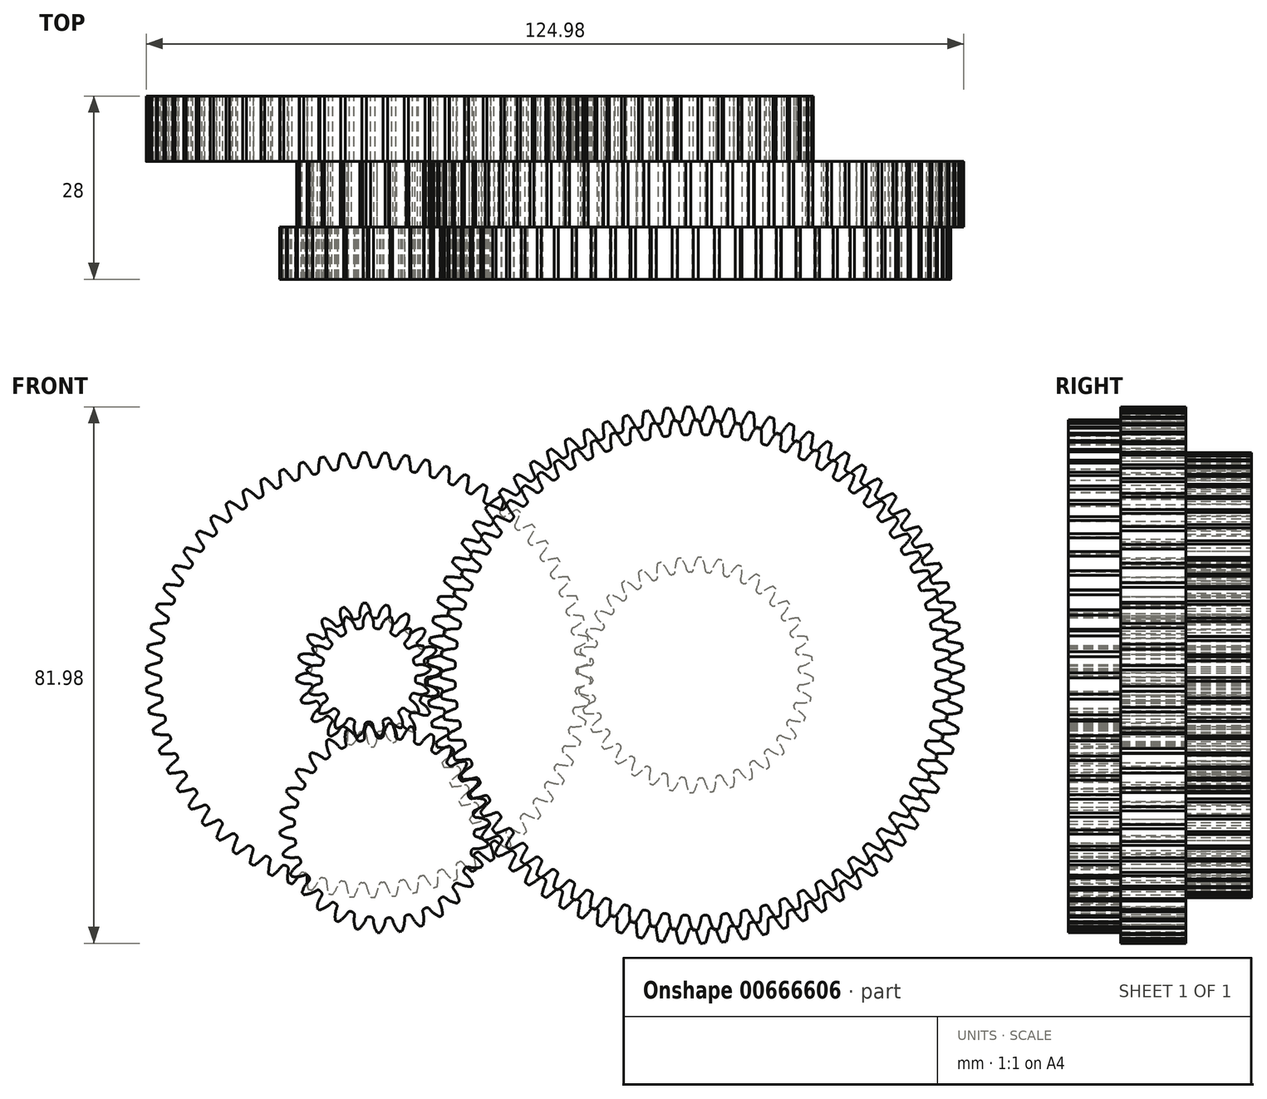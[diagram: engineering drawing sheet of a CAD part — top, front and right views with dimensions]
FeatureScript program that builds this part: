
annotation { "Feature Type Name" : "Feature", "Feature Type Description" : "" }
export const myFeature = defineFeature(function(context is Context, id is Id, definition is map)
    precondition{}
    {
        {
            var Q0;
            Q0=qCreatedBy(makeId("Front.planeOp"),FACE);
            var sketch = newSketch(context, id + "F0", { "sketchPlane" : qUnion([Q0])});
            skLineSegment(sketch, "E0", {"start": v(0, 0) * mm, "end": v(-50, 0) * mm, "construction": true});
            skLineSegment(sketch, "E1", {"start": v(-25, 25) * mm, "end": v(-25, -25) * mm, "construction": true});
            skPoint(sketch, "E2", {"position": v(-25, 0) * mm});
            skLineSegment(sketch, "E3", {"start": v(0, -50) * mm, "end": v(0, 50) * mm, "construction": true});
            skPoint(sketch, "E4", {"position": v(0, 0) * mm});
            skLineSegment(sketch, "E5.MirrorCS", {"start": v(25, 25) * mm, "end": v(25, -25) * mm, "construction": true});
            skLineSegment(sketch, "E6.MirrorCS", {"start": v(0, 0) * mm, "end": v(50, 0) * mm, "construction": true});
            skPoint(sketch, "E7.MirrorP", {"position": v(25, 0) * mm});
            skSolve(sketch);
        }
        {
            var Q0;
            Q0=qCreatedBy(makeId("Front.planeOp"),FACE);
            cPlane(context, id + "F1", {"entities" : qUnion([Q0]), "cplaneType" : CPlaneType.OFFSET, "offset" : 0 * mm, "width" : 150 * mm, "height" : 150 * mm});
        }
        {
            var Q0;
            Q0=qCreatedBy(makeId("Front.planeOp"),FACE);
            cPlane(context, id + "F2", {"entities" : qUnion([Q0]), "cplaneType" : CPlaneType.OFFSET, "offset" : 10 * mm, "width" : 150 * mm, "height" : 150 * mm});
        }
        {
            var Q0;
            Q0=qCreatedBy(id+"F2.planeOp",FACE);
            var sketch = newSketch(context, id + "F3", { "sketchPlane" : qUnion([Q0])});
            skCircle(sketch, "E8", {"center": v(25, 0) * mm, "radius": 17 * mm, "construction": true});
            skCircle(sketch, "E9", {"center": v(-25, 0) * mm, "radius": 33 * mm, "construction": true});
            skLineSegment(sketch, "E10", {"start": v(-25, 0) * mm, "end": v(-25, 41.53) * mm, "construction": true});
            skLineSegment(sketch, "E11", {"start": v(-25, 33) * mm, "end": v(-54.6, 33) * mm, "construction": true});
            skLineSegment(sketch, "E12", {"start": v(-25, 33) * mm, "end": v(-54.83, 22.14) * mm, "construction": true});
            skLineSegment(sketch, "E13", {"start": v(-35.6, 29.14) * mm, "end": v(-25, 0) * mm, "construction": true});
            skCircle(sketch, "E14", {"center": v(-25, 0) * mm, "radius": 31.75 * mm});
            skPoint(sketch, "E15", {"position": v(-25, 31.75) * mm});
            skPoint(sketch, "E16", {"position": v(-25, 34) * mm});
            skPoint(sketch, "E17", {"position": v(-25, 33.25) * mm});
            skLineSegment(sketch, "E18", {"start": v(-35.6, 29.14) * mm, "end": v(-25, 33.25) * mm, "construction": true});
            skPoint(sketch, "E19", {"position": v(-32.95, 30.17) * mm});
            skArc(sketch, "E20", {"start": v(-25.33, 34) * mm, "mid": v(-41.15, 27.8) * mm, "end": v(-24.46, 31) * mm, "construction": true});
            skArc(sketch, "E21", {"start": v(-24.46, 31) * mm, "mid": v(-24.76, 32.54) * mm, "end": v(-25.33, 34) * mm});
            skPoint(sketch, "E22", {"position": v(-24.9, 33) * mm});
            skPoint(sketch, "E23", {"position": v(-25.64, 33) * mm});
            skLineSegment(sketch, "E24", {"start": v(-25.64, 33) * mm, "end": v(-25, 0) * mm, "construction": true});
            skArc(sketch, "E25.MirrorCS", {"start": v(-26.74, 30.96) * mm, "mid": v(-26.5, 32.5) * mm, "end": v(-26, 33.99) * mm});
            skArc(sketch, "E26", {"start": v(-26, 33.99) * mm, "mid": v(-24.34, -34) * mm, "end": v(-25.33, 34) * mm, "construction": true});
            skArc(sketch, "E27", {"start": v(-25.33, 34) * mm, "mid": v(-25.66, 34) * mm, "end": v(-26, 33.99) * mm});
            skArc(sketch, "E28", {"start": v(-26.74, 30.96) * mm, "mid": v(-24.4, -31) * mm, "end": v(-24.46, 31) * mm});
            skArc(sketch, "E29", {"start": v(-24.46, 31) * mm, "mid": v(-25.6, 31) * mm, "end": v(-26.74, 30.96) * mm, "construction": true});
            skLineSegment(sketch, "E30", {"start": v(25, 0) * mm, "end": v(25, 21.62) * mm, "construction": true});
            skLineSegment(sketch, "E31", {"start": v(25, 17) * mm, "end": v(45.36, 17) * mm});
            skLineSegment(sketch, "E32", {"start": v(25, 17) * mm, "end": v(45.36, 9.59) * mm, "construction": true});
            skLineSegment(sketch, "E33", {"start": v(30.46, 15.01) * mm, "end": v(25, 0) * mm, "construction": true});
            skCircle(sketch, "E34", {"center": v(25, 0) * mm, "radius": 15.97 * mm, "construction": true});
            skPoint(sketch, "E35", {"position": v(25, 18) * mm});
            skPoint(sketch, "E36", {"position": v(25, 15.97) * mm});
            skPoint(sketch, "E37", {"position": v(25, 17.33) * mm});
            skLineSegment(sketch, "E38", {"start": v(25, 17.33) * mm, "end": v(30.46, 15.01) * mm, "construction": true});
            skPoint(sketch, "E39", {"position": v(29.1, 15.59) * mm});
            skPoint(sketch, "E40", {"position": v(24.88, 17) * mm});
            skPoint(sketch, "E41", {"position": v(25.61, 16.99) * mm});
            skLineSegment(sketch, "E42", {"start": v(25.61, 16.99) * mm, "end": v(25, 0) * mm, "construction": true});
            skArc(sketch, "E43", {"start": v(25.35, 18) * mm, "mid": v(24.85, 16.92) * mm, "end": v(24.65, 15.75) * mm});
            skArc(sketch, "E44", {"start": v(24.65, 15.75) * mm, "mid": v(33.34, 14.26) * mm, "end": v(25.35, 18) * mm, "construction": true});
            skArc(sketch, "E45.MirrorCS", {"start": v(25.94, 17.98) * mm, "mid": v(26.37, 16.86) * mm, "end": v(26.48, 15.68) * mm});
            skArc(sketch, "E46", {"start": v(25.94, 17.98) * mm, "mid": v(25.65, 17.99) * mm, "end": v(25.35, 18) * mm});
            skArc(sketch, "E47", {"start": v(25.35, 18) * mm, "mid": v(24.35, -17.99) * mm, "end": v(25.94, 17.98) * mm, "construction": true});
            skArc(sketch, "E48", {"start": v(24.65, 15.75) * mm, "mid": v(24.43, -15.74) * mm, "end": v(26.48, 15.68) * mm});
            skArc(sketch, "E49", {"start": v(26.48, 15.68) * mm, "mid": v(25.57, 15.74) * mm, "end": v(24.65, 15.75) * mm, "construction": true});
            skSolve(sketch);
        }
        {
            var Q0;
            Q0=makeQuery(id+"F3.imprint","IMPRINT",FACE,{"disambiguationData":[TD([[makeQuery(id+"F3.imprint","IMPRINT",EDGE,{"derivedFrom":sQuery(id+"F3.wireOp",EDGE,"E21")}),1.0]])]});
            var Q1;
            Q1=makeQuery(id+"F3.imprint","IMPRINT",FACE,{"disambiguationData":[TD([[makeQuery(id+"F3.imprint","IMPRINT",EDGE,{"derivedFrom":sQuery(id+"F3.wireOp",EDGE,"E43")}),1.0]])]});
            var Q2;
            {var subQ0=sQuery(id+"F3.wireOp",EDGE,"E28");Q2=makeQuery(id+"F3.imprint","IMPRINT",FACE,{"disambiguationData":[TD([[makeQuery(id+"F3.imprint","IMPRINT",EDGE,{"derivedFrom":subQ0}),-1.0]])]});}
            extrude(context, id + "F4", {"entities" : qUnion([Q0, Q1, Q2]), "depth" : 10 * mm, "offsetDistance" : 25 * mm});
        }
        {
            var Q0;
            Q0=makeQuery(id+"F4.opExtrude","SWEPT_EDGE",EDGE,{"disambiguationData":[OSD([sQuery(id+"F3.wireOp",EDGE,"E14"),sQuery(id+"F3.wireOp",EDGE,"E21")])]});
            var Q1;
            Q1=makeQuery(id+"F4.opExtrude","SWEPT_EDGE",EDGE,{"disambiguationData":[OSD([sQuery(id+"F3.wireOp",EDGE,"E14"),sQuery(id+"F3.wireOp",EDGE,"E25.MirrorCS")])]});
            var Q2;
            Q2=makeQuery(id+"F4.opExtrude","SWEPT_EDGE",EDGE,{"disambiguationData":[OSD([sQuery(id+"F3.wireOp",EDGE,"E45.MirrorCS"),sQuery(id+"F3.wireOp",EDGE,"E48")])]});
            var Q3;
            Q3=makeQuery(id+"F4.opExtrude","SWEPT_EDGE",EDGE,{"disambiguationData":[OSD([sQuery(id+"F3.wireOp",EDGE,"E43"),sQuery(id+"F3.wireOp",EDGE,"E48")])]});
            fillet(context, id + "F5", {"entities" : qUnion([Q0, Q1, Q2, Q3]), "radius" : 0.45 * mm, "tangentPropagation" : true, "allowEdgeOverflow" : false});
        }
        {
            var Q0;
            Q0=makeQuery(id+"F4.opExtrude","SWEPT_BODY",BODY,{"disambiguationData":[OSD([sQuery(id+"F3.wireOp",EDGE,"E43"),sQuery(id+"F3.wireOp",EDGE,"E45.MirrorCS"),sQuery(id+"F3.wireOp",EDGE,"E46"),sQuery(id+"F3.wireOp",EDGE,"E48")])]});
            var Q1;
            Q1=makeQuery(id+"F4.opExtrude","SWEPT_FACE",FACE,{"disambiguationData":[OSD([sQuery(id+"F3.wireOp",EDGE,"E48")])]});
            circularPattern(context, id + "F6", {"operationType" : NewBodyOperationType.ADD, "entities" : qUnion([Q0]), "axis" : qUnion([Q1]), "angle" : 360 * degree, "instanceCount" : 36, "equalSpace" : true});
        }
        {
            var Q0;
            Q0=makeQuery(id+"F4.opExtrude","SWEPT_BODY",BODY,{"disambiguationData":[OSD([sQuery(id+"F3.wireOp",EDGE,"E14"),sQuery(id+"F3.wireOp",EDGE,"E21"),sQuery(id+"F3.wireOp",EDGE,"E25.MirrorCS"),sQuery(id+"F3.wireOp",EDGE,"E27")])]});
            var Q1;
            Q1=makeQuery(id+"F4.opExtrude","SWEPT_FACE",FACE,{"disambiguationData":[OSD([sQuery(id+"F3.wireOp",EDGE,"E14")])]});
            circularPattern(context, id + "F7", {"operationType" : NewBodyOperationType.ADD, "entities" : qUnion([Q0]), "axis" : qUnion([Q1]), "angle" : 360 * degree, "instanceCount" : 66, "equalSpace" : true});
        }
        {
            var Q0;
            Q0=qCreatedBy(makeId("Front.planeOp"),FACE);
            cPlane(context, id + "F8", {"entities" : qUnion([Q0]), "cplaneType" : CPlaneType.OFFSET, "offset" : 20 * mm, "width" : 150 * mm, "height" : 150 * mm});
        }
        {
            var Q0;
            Q0=qCreatedBy(id+"F8.planeOp",FACE);
            var sketch = newSketch(context, id + "F9", { "sketchPlane" : qUnion([Q0])});
            skCircle(sketch, "E50", {"center": v(-25, 0) * mm, "radius": 10 * mm, "construction": true});
            skCircle(sketch, "E51", {"center": v(25, 0) * mm, "radius": 40 * mm, "construction": true});
            skLineSegment(sketch, "E52", {"start": v(-25, 0) * mm, "end": v(-25, 15.82) * mm, "construction": true});
            skLineSegment(sketch, "E53", {"start": v(-25, 10) * mm, "end": v(-43.04, 10) * mm, "construction": true});
            skLineSegment(sketch, "E54", {"start": v(-25, 10) * mm, "end": v(-43.04, 3.43) * mm, "construction": true});
            skCircle(sketch, "E55", {"center": v(-25, 0) * mm, "radius": 9.4 * mm, "construction": true});
            skLineSegment(sketch, "E56", {"start": v(-25, 0) * mm, "end": v(-28.21, 8.83) * mm, "construction": true});
            skPoint(sketch, "E57", {"position": v(-25, 11) * mm});
            skPoint(sketch, "E58", {"position": v(-25, 9.4) * mm});
            skPoint(sketch, "E59", {"position": v(-25, 10.47) * mm});
            skLineSegment(sketch, "E60", {"start": v(-25, 10.47) * mm, "end": v(-28.21, 8.83) * mm, "construction": true});
            skPoint(sketch, "E61", {"position": v(-27.41, 9.24) * mm});
            skArc(sketch, "E62", {"start": v(-25.35, 11) * mm, "mid": v(-30.02, 8.54) * mm, "end": v(-24.75, 8.75) * mm, "construction": true});
            skArc(sketch, "E63", {"start": v(-24.75, 8.75) * mm, "mid": v(-24.8, 9.94) * mm, "end": v(-25.35, 11) * mm});
            skPoint(sketch, "E64", {"position": v(-24.81, 10) * mm});
            skPoint(sketch, "E65", {"position": v(-25.55, 9.98) * mm});
            skLineSegment(sketch, "E66", {"start": v(-25.55, 9.98) * mm, "end": v(-25, 0) * mm, "construction": true});
            skArc(sketch, "E67.MirrorCS", {"start": v(-26.2, 8.67) * mm, "mid": v(-26.3, 9.86) * mm, "end": v(-25.86, 10.97) * mm});
            skArc(sketch, "E68", {"start": v(-26.2, 8.67) * mm, "mid": v(-24.52, -8.74) * mm, "end": v(-24.75, 8.75) * mm});
            skArc(sketch, "E69", {"start": v(-24.75, 8.75) * mm, "mid": v(-25.48, 8.74) * mm, "end": v(-26.2, 8.67) * mm, "construction": true});
            skArc(sketch, "E70", {"start": v(-25.35, 11) * mm, "mid": v(-25.6, 10.98) * mm, "end": v(-25.86, 10.97) * mm});
            skArc(sketch, "E71", {"start": v(-25.86, 10.97) * mm, "mid": v(-24.4, -10.98) * mm, "end": v(-25.35, 11) * mm, "construction": true});
            skLineSegment(sketch, "E72", {"start": v(25, 0) * mm, "end": v(26.56, 44.58) * mm, "construction": true});
            skLineSegment(sketch, "E73", {"start": v(26.4, 39.98) * mm, "end": v(67.67, 39.98) * mm, "construction": true});
            skLineSegment(sketch, "E74", {"start": v(26.4, 39.98) * mm, "end": v(67.67, 24.95) * mm, "construction": true});
            skLineSegment(sketch, "E75", {"start": v(38.01, 35.75) * mm, "end": v(25, 0) * mm, "construction": true});
            skCircle(sketch, "E76", {"center": v(25, 0) * mm, "radius": 38.75 * mm});
            skPoint(sketch, "E77", {"position": v(26.35, 38.73) * mm});
            skPoint(sketch, "E78", {"position": v(26.43, 40.98) * mm});
            skPoint(sketch, "E79", {"position": v(26.4, 40.23) * mm});
            skLineSegment(sketch, "E80", {"start": v(26.4, 40.23) * mm, "end": v(38.01, 35.75) * mm, "construction": true});
            skPoint(sketch, "E81", {"position": v(34.8, 36.99) * mm});
            skArc(sketch, "E82", {"start": v(26.73, 40.96) * mm, "mid": v(26.17, 39.54) * mm, "end": v(25.86, 38.03) * mm});
            skArc(sketch, "E83", {"start": v(25.86, 38.03) * mm, "mid": v(43.43, 34.44) * mm, "end": v(26.73, 40.96) * mm, "construction": true});
            skPoint(sketch, "E84", {"position": v(26.31, 39.98) * mm});
            skPoint(sketch, "E85", {"position": v(27.05, 39.95) * mm});
            skLineSegment(sketch, "E86", {"start": v(27.05, 39.95) * mm, "end": v(25, 0) * mm, "construction": true});
            skArc(sketch, "E87.MirrorCS", {"start": v(27.47, 40.93) * mm, "mid": v(27.88, 39.45) * mm, "end": v(28.03, 37.92) * mm});
            skArc(sketch, "E88", {"start": v(27.47, 40.93) * mm, "mid": v(27.1, 40.95) * mm, "end": v(26.73, 40.96) * mm});
            skArc(sketch, "E89", {"start": v(26.73, 40.96) * mm, "mid": v(22.9, -40.95) * mm, "end": v(27.47, 40.93) * mm, "construction": true});
            skArc(sketch, "E90", {"start": v(25.86, 38.03) * mm, "mid": v(23.05, -38) * mm, "end": v(28.03, 37.92) * mm});
            skArc(sketch, "E91", {"start": v(28.03, 37.92) * mm, "mid": v(26.95, 38) * mm, "end": v(25.86, 38.03) * mm, "construction": true});
            skLineSegment(sketch, "E92", {"start": v(-25, 0) * mm, "end": v(25, 0) * mm});
            skSolve(sketch);
        }
        {
            var Q0;
            Q0=makeQuery(id+"F9.imprint","IMPRINT",FACE,{"disambiguationData":[TD([[makeQuery(id+"F9.imprint","IMPRINT",EDGE,{"derivedFrom":sQuery(id+"F9.wireOp",EDGE,"E63")}),1.0]])]});
            var Q1;
            Q1=makeQuery(id+"F9.imprint","IMPRINT",FACE,{"disambiguationData":[TD([[makeQuery(id+"F9.imprint","IMPRINT",EDGE,{"derivedFrom":sQuery(id+"F9.wireOp",EDGE,"E82")}),1.0]])]});
            var Q2;
            {var subQ0=sQuery(id+"F9.wireOp",EDGE,"E90");Q2=makeQuery(id+"F9.imprint","IMPRINT",FACE,{"disambiguationData":[TD([[makeQuery(id+"F9.imprint","IMPRINT",EDGE,{"derivedFrom":subQ0}),-1.0]])]});}
            var Q3;
            {var subQ1=sQuery(id+"F9.wireOp",EDGE,"E82");var subQ6=sQuery(id+"F9.wireOp",EDGE,"E76");var subQ8=makeQuery(id+"F9.imprint","INTERSECT",VERTEX,{"derivedFrom":[subQ6,subQ1]});Q3=makeQuery(id+"F9.imprint","IMPRINT",FACE,{"disambiguationData":[TD([[makeQuery(id+"F9.imprint","IMPRINT",EDGE,{"disambiguationData":[TD([[subQ8,1.0]])],"derivedFrom":subQ6}),1.0]])]});}
            extrude(context, id + "F10", {"entities" : qUnion([Q0, Q1, Q2, Q3]), "depth" : 10 * mm, "offsetDistance" : 25 * mm});
        }
        {
            var Q0;
            Q0=makeQuery(id+"F10.opExtrude","SWEPT_EDGE",EDGE,{"disambiguationData":[OSD([sQuery(id+"F9.wireOp",EDGE,"E67.MirrorCS"),sQuery(id+"F9.wireOp",EDGE,"E68")])]});
            var Q1;
            Q1=makeQuery(id+"F10.opExtrude","SWEPT_EDGE",EDGE,{"disambiguationData":[OSD([sQuery(id+"F9.wireOp",EDGE,"E63"),sQuery(id+"F9.wireOp",EDGE,"E68")])]});
            var Q2;
            Q2=makeQuery(id+"F10.opExtrude","SWEPT_EDGE",EDGE,{"disambiguationData":[OSD([sQuery(id+"F9.wireOp",EDGE,"E76"),sQuery(id+"F9.wireOp",EDGE,"E82")])]});
            var Q3;
            Q3=makeQuery(id+"F10.opExtrude","SWEPT_EDGE",EDGE,{"disambiguationData":[OSD([sQuery(id+"F9.wireOp",EDGE,"E76"),sQuery(id+"F9.wireOp",EDGE,"E87.MirrorCS")])]});
            fillet(context, id + "F11", {"entities" : qUnion([Q0, Q1, Q2, Q3]), "radius" : 0.45 * mm, "tangentPropagation" : true, "allowEdgeOverflow" : false});
        }
        {
            var Q0;
            Q0=makeQuery(id+"F10.opExtrude","SWEPT_BODY",BODY,{"disambiguationData":[OSD([sQuery(id+"F9.wireOp",EDGE,"E63"),sQuery(id+"F9.wireOp",EDGE,"E67.MirrorCS"),sQuery(id+"F9.wireOp",EDGE,"E68"),sQuery(id+"F9.wireOp",EDGE,"E70")])]});
            var Q1;
            Q1=makeQuery(id+"F10.opExtrude","SWEPT_FACE",FACE,{"disambiguationData":[OSD([sQuery(id+"F9.wireOp",EDGE,"E68")])]});
            circularPattern(context, id + "F12", {"operationType" : NewBodyOperationType.ADD, "entities" : qUnion([Q0]), "axis" : qUnion([Q1]), "angle" : 360 * degree, "instanceCount" : 20, "equalSpace" : true});
        }
        {
            var Q0;
            Q0=makeQuery(id+"F10.opExtrude","SWEPT_BODY",BODY,{"disambiguationData":[OSD([sQuery(id+"F9.wireOp",EDGE,"E76"),sQuery(id+"F9.wireOp",EDGE,"E82"),sQuery(id+"F9.wireOp",EDGE,"E87.MirrorCS"),sQuery(id+"F9.wireOp",EDGE,"E88")])]});
            var Q1;
            Q1=makeQuery(id+"F10.opExtrude","SWEPT_FACE",FACE,{"disambiguationData":[OSD([sQuery(id+"F9.wireOp",EDGE,"E76")])]});
            circularPattern(context, id + "F13", {"operationType" : NewBodyOperationType.ADD, "entities" : qUnion([Q0]), "axis" : qUnion([Q1]), "angle" : 360 * degree, "instanceCount" : 80, "equalSpace" : true});
        }
        {
            var Q0;
            Q0=qCreatedBy(makeId("Front.planeOp"),FACE);
            cPlane(context, id + "F14", {"entities" : qUnion([Q0]), "cplaneType" : CPlaneType.OFFSET, "offset" : 30 * mm, "width" : 150 * mm, "height" : 150 * mm});
        }
        {
            var Q0;
            Q0=qCreatedBy(id+"F14.planeOp",FACE);
            var sketch = newSketch(context, id + "F15", { "sketchPlane" : qUnion([Q0])});
            skCircle(sketch, "E93", {"center": v(-25, 0) * mm, "radius": 8.5 * mm, "construction": true});
            skCircle(sketch, "E94", {"center": v(25, 0) * mm, "radius": 38 * mm, "construction": true});
            skCircle(sketch, "E95", {"center": v(-22.57, -23.37) * mm, "radius": 15 * mm, "construction": true});
            skLineSegment(sketch, "E96", {"start": v(25, 0) * mm, "end": v(28.14, 47.86) * mm, "construction": true});
            skLineSegment(sketch, "E97", {"start": v(27.49, 37.92) * mm, "end": v(52.67, 37.92) * mm, "construction": true});
            skLineSegment(sketch, "E98", {"start": v(27.49, 37.92) * mm, "end": v(56.54, 27.34) * mm, "construction": true});
            skLineSegment(sketch, "E99", {"start": v(25, 0) * mm, "end": v(37.48, 34.28) * mm});
            skCircle(sketch, "E100", {"center": v(25, 0) * mm, "radius": 36.75 * mm});
            skPoint(sketch, "E101", {"position": v(27.55, 38.92) * mm});
            skPoint(sketch, "E102", {"position": v(27.55, 36.66) * mm});
            skLineSegment(sketch, "E103", {"start": v(27.55, 38.92) * mm, "end": v(27.55, 36.66) * mm, "construction": true});
            skPoint(sketch, "E104", {"position": v(27.55, 38.17) * mm});
            skPoint(sketch, "E105", {"position": v(34.4, 35.4) * mm});
            skArc(sketch, "E106", {"start": v(27.9, 38.9) * mm, "mid": v(27.38, 37.7) * mm, "end": v(27.08, 36.42) * mm});
            skArc(sketch, "E107", {"start": v(27.08, 36.42) * mm, "mid": v(41.43, 33.1) * mm, "end": v(27.9, 38.9) * mm, "construction": true});
            skPoint(sketch, "E108", {"position": v(27.46, 37.92) * mm});
            skPoint(sketch, "E109", {"position": v(28.2, 37.87) * mm});
            skLineSegment(sketch, "E110", {"start": v(28.2, 37.87) * mm, "end": v(25, 0) * mm, "construction": true});
            skArc(sketch, "E111.MirrorCS", {"start": v(28.66, 38.83) * mm, "mid": v(28.97, 37.56) * mm, "end": v(29.04, 36.26) * mm});
            skArc(sketch, "E112", {"start": v(27.9, 38.9) * mm, "mid": v(21.72, -38.86) * mm, "end": v(28.66, 38.83) * mm, "construction": true});
            skArc(sketch, "E113", {"start": v(28.66, 38.83) * mm, "mid": v(28.28, 38.86) * mm, "end": v(27.9, 38.9) * mm});
            skLineSegment(sketch, "E114", {"start": v(27.08, 36.42) * mm, "end": v(27.08, 36.42) * mm});
            skArc(sketch, "E115", {"start": v(29.04, 36.26) * mm, "mid": v(28.06, 36.35) * mm, "end": v(27.08, 36.42) * mm, "construction": true});
            skArc(sketch, "E116", {"start": v(27.08, 36.42) * mm, "mid": v(27.02, 36.43) * mm, "end": v(26.96, 36.43) * mm});
            skArc(sketch, "E117", {"start": v(26.96, 36.43) * mm, "mid": v(22, -36.36) * mm, "end": v(29.04, 36.26) * mm});
            skLineSegment(sketch, "E118", {"start": v(-22.57, -23.37) * mm, "end": v(-22.57, -47.46) * mm, "construction": true});
            skLineSegment(sketch, "E119", {"start": v(-22.57, -47.46) * mm, "end": v(-22.57, -38.37) * mm, "construction": true});
            skLineSegment(sketch, "E120", {"start": v(-22.57, -38.37) * mm, "end": v(-48.76, -38.37) * mm, "construction": true});
            skLineSegment(sketch, "E121", {"start": v(-22.57, -38.37) * mm, "end": v(-52.03, -27.65) * mm, "construction": true});
            skLineSegment(sketch, "E122", {"start": v(-22.57, -23.37) * mm, "end": v(-27.39, -36.62) * mm, "construction": true});
            skCircle(sketch, "E123", {"center": v(-22.57, -23.37) * mm, "radius": 14.1 * mm, "construction": true});
            skPoint(sketch, "E124", {"position": v(-22.57, -37.47) * mm});
            skPoint(sketch, "E125", {"position": v(-22.57, -39.37) * mm});
            skPoint(sketch, "E126", {"position": v(-22.57, -38.1) * mm});
            skLineSegment(sketch, "E127", {"start": v(-27.39, -36.62) * mm, "end": v(-22.57, -38.1) * mm, "construction": true});
            skPoint(sketch, "E128", {"position": v(-26.18, -37) * mm});
            skArc(sketch, "E129", {"start": v(-22.4, -37.12) * mm, "mid": v(-29.73, -35.67) * mm, "end": v(-23.23, -39.36) * mm, "construction": true});
            skArc(sketch, "E130", {"start": v(-23.23, -39.36) * mm, "mid": v(-22.64, -38.3) * mm, "end": v(-22.4, -37.12) * mm});
            skPoint(sketch, "E131", {"position": v(-23.4, -38.35) * mm});
            skPoint(sketch, "E132", {"position": v(-22.66, -38.37) * mm});
            skLineSegment(sketch, "E133", {"start": v(-23.4, -38.35) * mm, "end": v(-22.57, -23.37) * mm, "construction": true});
            skArc(sketch, "E134.MirrorCS", {"start": v(-23.67, -39.34) * mm, "mid": v(-24.15, -38.22) * mm, "end": v(-24.25, -37.02) * mm});
            skArc(sketch, "E135", {"start": v(-24.25, -37.02) * mm, "mid": v(-23.33, -37.1) * mm, "end": v(-22.4, -37.12) * mm, "construction": true});
            skArc(sketch, "E136", {"start": v(-22.4, -37.12) * mm, "mid": v(-21.8, -9.64) * mm, "end": v(-24.25, -37.02) * mm});
            skArc(sketch, "E137", {"start": v(-23.23, -39.36) * mm, "mid": v(-21.68, -7.4) * mm, "end": v(-23.67, -39.34) * mm, "construction": true});
            skArc(sketch, "E138", {"start": v(-23.67, -39.34) * mm, "mid": v(-23.45, -39.35) * mm, "end": v(-23.23, -39.36) * mm});
            skLineSegment(sketch, "E139", {"start": v(-25, 0) * mm, "end": v(-38.6, 0) * mm, "construction": true});
            skLineSegment(sketch, "E140", {"start": v(-33.5, 0) * mm, "end": v(-33.5, 8.6) * mm, "construction": true});
            skLineSegment(sketch, "E141", {"start": v(-33.5, 0) * mm, "end": v(-30.37, 8.6) * mm, "construction": true});
            skLineSegment(sketch, "E142", {"start": v(-25, 0) * mm, "end": v(-32.5, 2.73) * mm, "construction": true});
            skCircle(sketch, "E143", {"center": v(-25, 0) * mm, "radius": 7.99 * mm, "construction": true});
            skPoint(sketch, "E144", {"position": v(-32.99, 0) * mm});
            skPoint(sketch, "E145", {"position": v(-34.5, 0) * mm});
            skPoint(sketch, "E146", {"position": v(-33.5, 0) * mm});
            skLineSegment(sketch, "E147", {"start": v(-33.5, 0) * mm, "end": v(-32.5, 2.73) * mm});
            skPoint(sketch, "E148", {"position": v(-32.75, 2.05) * mm});
            skArc(sketch, "E149", {"start": v(-34.47, 0.71) * mm, "mid": v(-33.45, -0.01) * mm, "end": v(-32.2, -0.06) * mm});
            skArc(sketch, "E150", {"start": v(-32.2, -0.06) * mm, "mid": v(-32.05, 4.11) * mm, "end": v(-34.47, 0.71) * mm, "construction": true});
            skPoint(sketch, "E151", {"position": v(-33.47, 0.74) * mm});
            skLineSegment(sketch, "E152", {"start": v(-33.47, 0.74) * mm, "end": v(-25, 0) * mm, "construction": true});
            skArc(sketch, "E153.MirrorCS", {"start": v(-34.45, 0.93) * mm, "mid": v(-33.32, 1.47) * mm, "end": v(-32.08, 1.3) * mm});
            skArc(sketch, "E154", {"start": v(-34.45, 0.93) * mm, "mid": v(-34.46, 0.82) * mm, "end": v(-34.47, 0.71) * mm});
            skArc(sketch, "E155", {"start": v(-34.47, 0.71) * mm, "mid": v(-15.54, -0.82) * mm, "end": v(-34.45, 0.93) * mm, "construction": true});
            skArc(sketch, "E156", {"start": v(-32.08, 1.3) * mm, "mid": v(-32.17, 0.62) * mm, "end": v(-32.2, -0.06) * mm, "construction": true});
            skArc(sketch, "E157", {"start": v(-32.2, -0.06) * mm, "mid": v(-17.83, -0.62) * mm, "end": v(-32.08, 1.3) * mm});
            skLineSegment(sketch, "E158", {"start": v(-25, 0) * mm, "end": v(-32.07, 1.36) * mm, "construction": true});
            skLineSegment(sketch, "E159.trimOffspring", {"start": v(-32.94, 1.53) * mm, "end": v(-32.94, 1.53) * mm});
            skLineSegment(sketch, "E160", {"start": v(-32.07, 1.36) * mm, "end": v(-32.58, 1.46) * mm});
            skLineSegment(sketch, "E161.MirrorCS", {"start": v(-32.2, -0.12) * mm, "end": v(-32.72, -0.13) * mm});
            skLineSegment(sketch, "E162", {"start": v(-25, 0) * mm, "end": v(25, 0) * mm});
            skSolve(sketch);
        }
        {
            var Q0;
            Q0 = qSketchRegion(id + "F15", true);
            var Q1;
            {var subQ6=sQuery(id+"F15.wireOp",EDGE,"E117");Q1=makeQuery(id+"F15.imprint","IMPRINT",FACE,{"disambiguationData":[TD([[makeQuery(id+"F15.imprint","IMPRINT",EDGE,{"derivedFrom":subQ6}),1.0]])]});}
            extrude(context, id + "F16", {"entities" : qUnion([Q0, Q1]), "depth" : 8 * mm, "offsetDistance" : 25 * mm});
        }
        {
            var Q0;
            Q0=makeQuery(id+"F16.opExtrude","SWEPT_EDGE",EDGE,{"disambiguationData":[OSD([sQuery(id+"F15.wireOp",EDGE,"E100"),sQuery(id+"F15.wireOp",EDGE,"E106")])]});
            var Q1;
            Q1=makeQuery(id+"F16.opExtrude","SWEPT_EDGE",EDGE,{"disambiguationData":[OSD([sQuery(id+"F15.wireOp",EDGE,"E157"),sQuery(id+"F15.wireOp",EDGE,"E161.MirrorCS")])]});
            var Q2;
            Q2=makeQuery(id+"F16.opExtrude","SWEPT_EDGE",EDGE,{"disambiguationData":[OSD([sQuery(id+"F15.wireOp",EDGE,"E130"),sQuery(id+"F15.wireOp",EDGE,"E136")])]});
            var Q3;
            Q3=makeQuery(id+"F16.opExtrude","SWEPT_EDGE",EDGE,{"disambiguationData":[OSD([sQuery(id+"F15.wireOp",EDGE,"E134.MirrorCS"),sQuery(id+"F15.wireOp",EDGE,"E136")])]});
            var Q4;
            Q4=makeQuery(id+"F16.opExtrude","SWEPT_EDGE",EDGE,{"disambiguationData":[OSD([sQuery(id+"F15.wireOp",EDGE,"E100"),sQuery(id+"F15.wireOp",EDGE,"E111.MirrorCS")])]});
            var Q5;
            Q5=makeQuery(id+"F16.opExtrude","SWEPT_EDGE",EDGE,{"disambiguationData":[OSD([sQuery(id+"F15.wireOp",EDGE,"E157"),sQuery(id+"F15.wireOp",EDGE,"E160")])]});
            fillet(context, id + "F17", {"entities" : qUnion([Q0, Q1, Q2, Q3, Q4, Q5]), "radius" : 0.45 * mm, "tangentPropagation" : true, "allowEdgeOverflow" : false});
        }
        {
            var Q0;
            Q0=makeQuery(id+"F16.opExtrude","SWEPT_BODY",BODY,{"disambiguationData":[OSD([sQuery(id+"F15.wireOp",EDGE,"E149"),sQuery(id+"F15.wireOp",EDGE,"E153.MirrorCS"),sQuery(id+"F15.wireOp",EDGE,"E154"),sQuery(id+"F15.wireOp",EDGE,"E157"),sQuery(id+"F15.wireOp",EDGE,"E160"),sQuery(id+"F15.wireOp",EDGE,"E161.MirrorCS")])]});
            var Q1;
            Q1=makeQuery(id+"F16.opExtrude","SWEPT_FACE",FACE,{"disambiguationData":[OSD([sQuery(id+"F15.wireOp",EDGE,"E157")])]});
            circularPattern(context, id + "F18", {"operationType" : NewBodyOperationType.ADD, "entities" : qUnion([Q0]), "axis" : qUnion([Q1]), "angle" : 360 * degree, "instanceCount" : 17, "equalSpace" : true});
        }
        {
            var Q0;
            Q0=makeQuery(id+"F16.opExtrude","SWEPT_BODY",BODY,{"disambiguationData":[OSD([sQuery(id+"F15.wireOp",EDGE,"E130"),sQuery(id+"F15.wireOp",EDGE,"E134.MirrorCS"),sQuery(id+"F15.wireOp",EDGE,"E136"),sQuery(id+"F15.wireOp",EDGE,"E138")])]});
            var Q1;
            Q1=makeQuery(id+"F16.opExtrude","SWEPT_FACE",FACE,{"disambiguationData":[OSD([sQuery(id+"F15.wireOp",EDGE,"E136")])]});
            circularPattern(context, id + "F19", {"operationType" : NewBodyOperationType.ADD, "entities" : qUnion([Q0]), "axis" : qUnion([Q1]), "angle" : 360 * degree, "instanceCount" : 30, "equalSpace" : true});
        }
        {
            var Q0;
            Q0=makeQuery(id+"F16.opExtrude","SWEPT_BODY",BODY,{"disambiguationData":[OSD([sQuery(id+"F15.wireOp",EDGE,"E106"),sQuery(id+"F15.wireOp",EDGE,"E111.MirrorCS"),sQuery(id+"F15.wireOp",EDGE,"E113"),sQuery(id+"F15.wireOp",EDGE,"E116")])]});
            var Q1;
            Q1=makeQuery(id+"F16.opExtrude","SWEPT_FACE",FACE,{"disambiguationData":[OSD([sQuery(id+"F15.wireOp",EDGE,"E100")])]});
            circularPattern(context, id + "F20", {"operationType" : NewBodyOperationType.ADD, "entities" : qUnion([Q0]), "axis" : qUnion([Q1]), "angle" : 360 * degree, "instanceCount" : 76, "equalSpace" : true});
        }
    });
